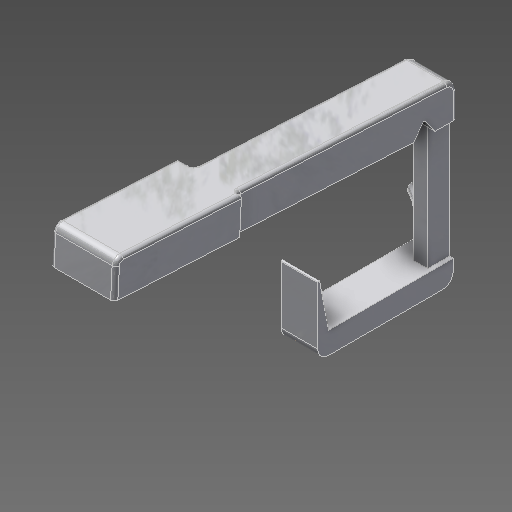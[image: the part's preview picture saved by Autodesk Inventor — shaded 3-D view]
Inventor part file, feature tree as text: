
AUTODESK INVENTOR PART (.ipt)
format: ipt  version: 2020 (Build 240168000, 168)  size: 332,800 bytes
history: native  units: mm
features: extrude x7, fillet x7, other x3, draft x1, chamfer x1
ambient origin geometry x8: Origin, YZ Plane, XZ Plane, XY Plane, X Axis, Y Axis, Z Axis, Center Point
bodies: Solid1 (feature_tree)
feature tree (19):
  other  "Key Sketch"
  extrude  "Upper Key"  Depth=10.0mm
  extrude  "Lower Key"  Depth=1.0mm
  other  "Hinge Cut Sketch"
  extrude  "Hinge Cut"  Depth=10.0mm TaperAngle=0.0deg
  extrude  "Hinge Cut 2"  Depth=3.0mm
  other  "Lever Sketch"
  extrude  "Vertical Lever"  Depth=3.0mm
  extrude  "Horizontal Lever"  Depth=33.6625mm
  extrude  "Spring Hook"  Depth=0.5mm
  draft  "FaceDraft3"
  chamfer  "Chamfer1"  Distance=3.0mm
  fillet  "Fillet9"  Radius=6.0mm
  fillet  "Fillet10"  Radius=4.0mm
  fillet  "Fillet5"  Radius=10.0mm
  fillet  "Fillet4"  [1 undecoded]
  fillet  "Fillet11"  Radius=3.0mm
  fillet  "Fillet15"  Radius=2.3mm
  fillet  "Fillet14"  Radius=5.3mm
note: 1 required parameter value undecoded (feature->parameter linkage not recoverable at this tier; creation-order binding heuristic only, values carry confidence <= 0.55)
